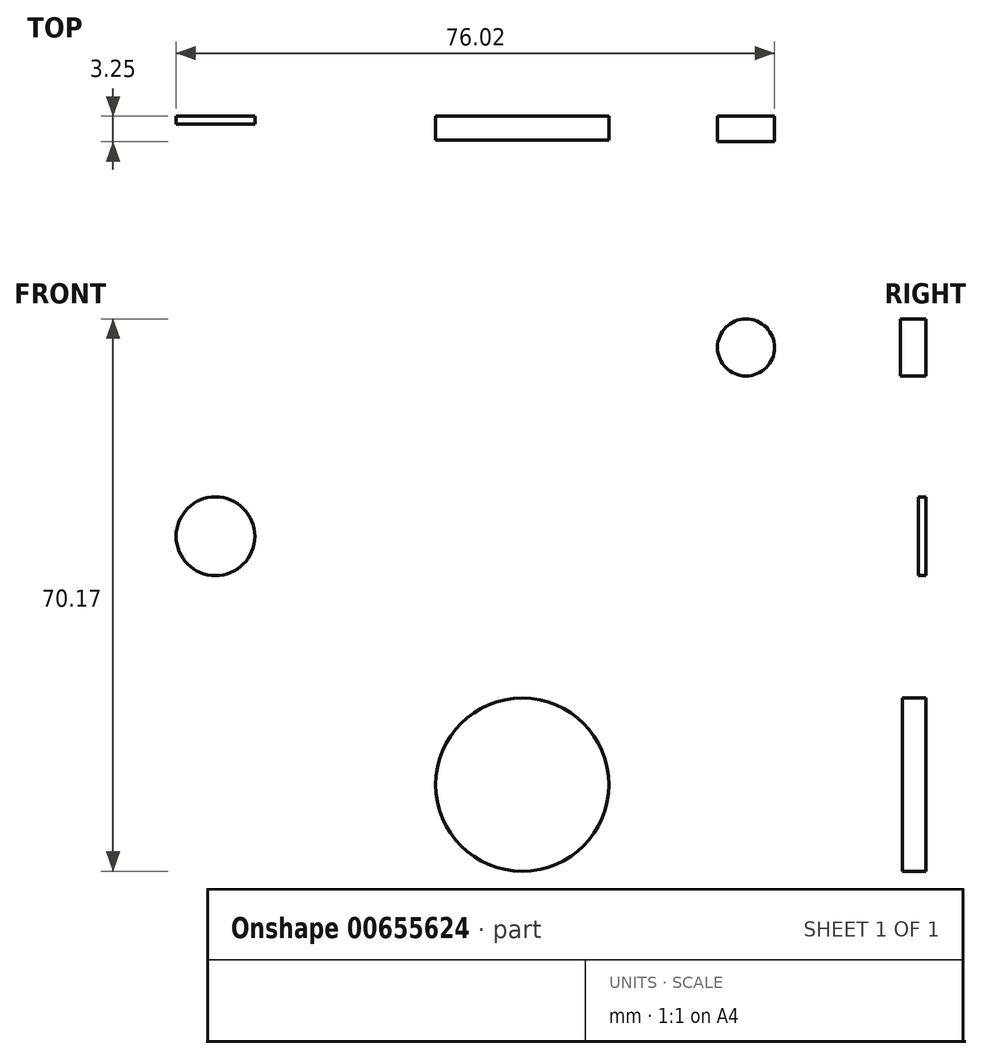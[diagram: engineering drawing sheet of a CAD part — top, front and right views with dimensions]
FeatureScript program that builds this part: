
annotation { "Feature Type Name" : "Feature", "Feature Type Description" : "" }
export const myFeature = defineFeature(function(context is Context, id is Id, definition is map)
    precondition{}
    {
        {
            var Q0;
            Q0=qCreatedBy(makeId("Front.planeOp"),FACE);
            var sketch = newSketch(context, id + "F0", { "sketchPlane" : qUnion([Q0])});
            skCircle(sketch, "E0", {"center": v(0, 0) * mm, "radius": 11 * mm});
            skCircle(sketch, "E1", {"center": v(28.41, 55.54) * mm, "radius": 3.62 * mm});
            skCircle(sketch, "E2", {"center": v(-38.98, 31.56) * mm, "radius": 5 * mm});
            skSolve(sketch);
        }
        {
            var Q0;
            Q0=makeQuery(id+"F0.imprint","IMPRINT",FACE,{"disambiguationData":[TD([[makeQuery(id+"F0.imprint","IMPRINT",EDGE,{"derivedFrom":sQuery(id+"F0.wireOp",EDGE,"E0")}),1.0]])]});
            var Q1;
            Q1=sQuery(id+"F0.wireOp",EDGE,"E0");
            extrude(context, id + "F1", {"entities" : qUnion([Q0]), "surfaceEntities" : qUnion([Q1]), "depth" : 3 * mm, "offsetDistance" : 25.4 * mm});
        }
        {
            var Q0;
            Q0=makeQuery(id+"F0.imprint","IMPRINT",FACE,{"disambiguationData":[TD([[makeQuery(id+"F0.imprint","IMPRINT",EDGE,{"derivedFrom":sQuery(id+"F0.wireOp",EDGE,"E2")}),1.0]])]});
            extrude(context, id + "F2", {"entities" : qUnion([Q0]), "depth" : 1 * mm, "offsetDistance" : 25.4 * mm});
        }
        {
            var Q0;
            Q0=makeQuery(id+"F0.imprint","IMPRINT",FACE,{"disambiguationData":[TD([[makeQuery(id+"F0.imprint","IMPRINT",EDGE,{"derivedFrom":sQuery(id+"F0.wireOp",EDGE,"E1")}),1.0]])]});
            extrude(context, id + "F3", {"entities" : qUnion([Q0]), "depth" : 3.25 * mm, "offsetDistance" : 25.4 * mm});
        }
    });
